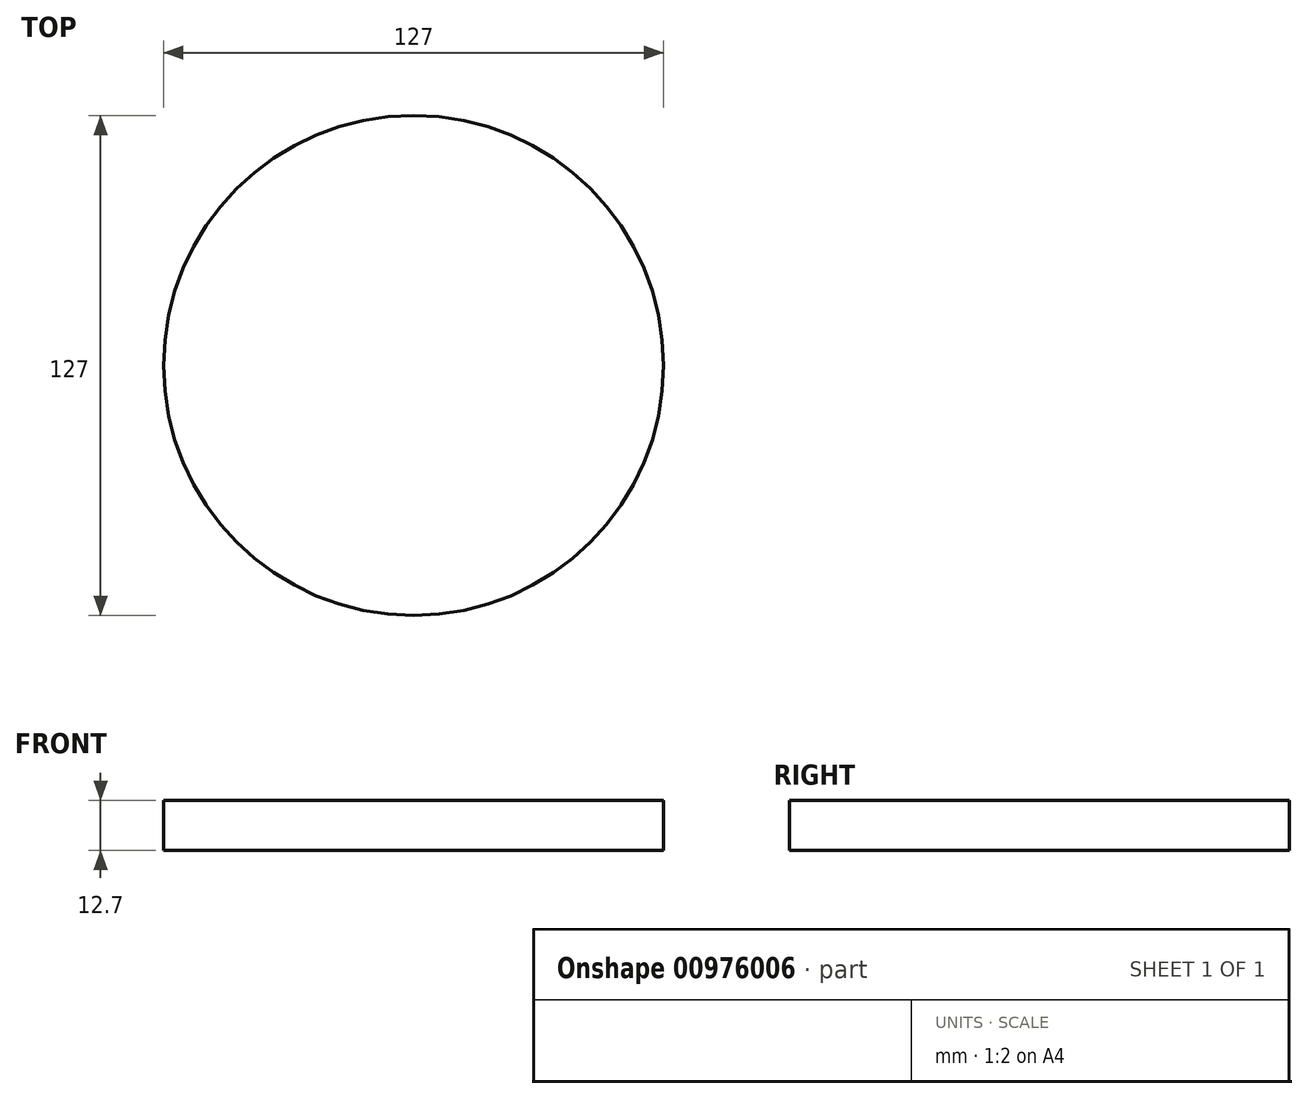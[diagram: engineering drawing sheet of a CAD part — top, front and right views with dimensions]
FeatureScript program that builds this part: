
annotation { "Feature Type Name" : "Feature", "Feature Type Description" : "" }
export const myFeature = defineFeature(function(context is Context, id is Id, definition is map)
    precondition{}
    {
        {
            var Q0;
            Q0=qCreatedBy(makeId("Top.planeOp"),FACE);
            var sketch = newSketch(context, id + "F0", { "sketchPlane" : qUnion([Q0])});
            skCircle(sketch, "E0", {"center": v(0, 0) * mm, "radius": 63.5 * mm});
            skSolve(sketch);
        }
        {
            var Q0;
            Q0=qSketchRegion(id+"F0",true);
            extrude(context, id + "F1", {"entities" : qUnion([Q0]), "depth" : 12.7 * mm, "offsetDistance" : 25.4 * mm});
        }
    });
